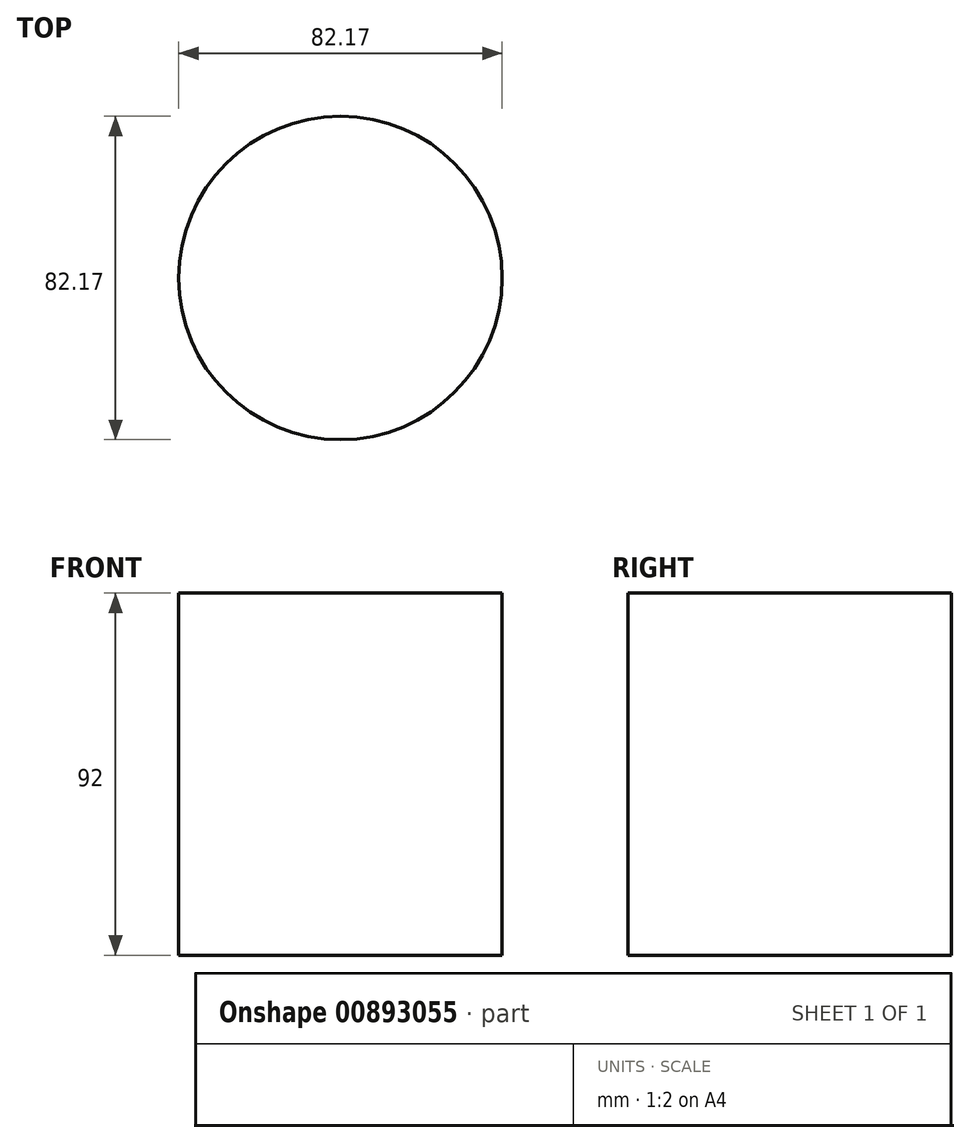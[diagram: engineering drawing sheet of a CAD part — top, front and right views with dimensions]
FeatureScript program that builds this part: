
annotation { "Feature Type Name" : "Feature", "Feature Type Description" : "" }
export const myFeature = defineFeature(function(context is Context, id is Id, definition is map)
    precondition{}
    {
        {
            var Q0;
            Q0=qCreatedBy(makeId("Top.planeOp"),FACE);
            var sketch = newSketch(context, id + "F0", { "sketchPlane" : qUnion([Q0])});
            skCircle(sketch, "E0", {"center": v(-2.19, -11.06) * mm, "radius": 41.09 * mm});
            skSolve(sketch);
        }
        {
            var Q0;
            Q0 = qSketchRegion(id + "F0", true);
            extrude(context, id + "F1", {"entities" : qUnion([Q0]), "depth" : 92 * mm, "offsetDistance" : 25 * mm});
        }
    });
